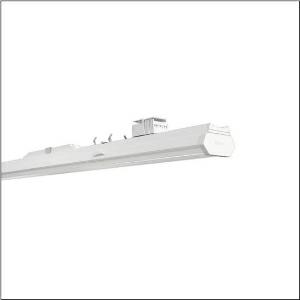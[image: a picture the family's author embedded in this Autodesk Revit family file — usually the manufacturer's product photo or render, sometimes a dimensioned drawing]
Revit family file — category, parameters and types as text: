
# Revit family: licross_r__11_protected_mo_51td1bdn59xg_8de8
name_source: partatom
category: Lighting Fixtures
units: mm (PartAtom-declared; Revit-internal decimal feet)

## family parameters
Cut with Voids When Loaded = No
Host = Face
Light Source = No
Part Type = Normal
Room Calculation Point = No
Round Connector Dimension = Use Diameter
Shared = No

## types (1)
- --- (1 x LED, 9230 lm, 57.1 W, 5000K)
    Apparent Load = 57 VA
    CIE Flux Codes = 54 82 95 97 100
    Color Rendering = 80
    Color Temperature = 5000K
    Default Elevation = 1800 mm
    Description = Licross® 11 Protected MO, luminaire insert, of sheet steel, galvanised, coil coated, white, length: 1.500mm, width: 90mm, height: 101mm, LED rated luminous flux: 9.230lm, light colour: 850, control gear: DALI 2, with plug, 5-pole, with phase selection, mains connection: 220..240V, AC, 50/60Hz, rated input power: 57W, internal wiring halogen-free, primary optical cover: cover, of PMMA, light emission: direct distribution, primary light characteristic: symmetric, protection rating (complete): IP54, insulation class (complete): insulation class I (protective earthing), certification: CE, ENEC, VDE, UKCA, protection symbol: D if used in an environment with non-conductive dust loads with corresponding accessories, impact resistance: IK06, permissible ambient temperature for indoor applications: -25..+35°C, corresponds to IFS (International Featured Standards) requirements for safety and quality in the food industry, reducing of maximum allowable ambient temperature of 5°C with ceiling mounting, LABS conformity tested according to VDMA 24364:2018-05, packaging unit: 1 piece
    Height = 92 mm
    Lamp = 1 x LED
    Lamp Light Flux = 9230 lm
    Lamp Power = 57.1 W
    Lamp count = 1
    Length = 1500 mm
    Luminous efficacy = 162 lm/W
    Manufacturer = Siteco
    ModVariant = No
    Model = 51TD1BDN59XG
    Mounting Place = Ceiling
    Mounting Type = Pendant
    Number of Poles = 1
    OnlyDefault = Yes
    Power Factor = 1
    Product Name = Licross® 11 Protected MO
    Product group = luminaire insert | ceiling pendant
    ProductGroupID = 902
    Protection Class = Protection class I
    Protection Degree = IP 54
    RLX_Detail_Level = 1
    RLX_Emergency_Light_Flux = 0 lm
    RLX_Emergency_Type = 0
    RLX_Emergency_Type_DB = No
    RlxData = <blob elided: 24385 chars, md5=a6683bd3>
    Socket = socket
    Standby Power = 0 W
    System Light Flux = 9230 lm
    System Power = 57 W
    Type Comments = factory setting: luminous flux: 100 % | dim-lin: 254 | 378 mA
    Type Image = l_1256145.jpg
    URL = http://relux.com
    VarID = @adj_018779
    Voltage = 0 V
    Weight = 0.00 kg
    Width = 88 mm

## geometry (parser evidence)
native form markers: Blend x4, Sweep x11
no freeform markers — native parametric forms only
